# Revit family: HVAC_Fireplaces_Regency-Fireplace_Seattle-Gas-Fireplace_CST50E-3
name_source: partatom
category: Specialty Equipment
units: mm (PartAtom-declared; Revit-internal decimal feet)

## family parameters
Cut with Voids When Loaded = No
Host = Face
Maintain Annotation Orientation = No
OmniClass Number = 23.40.20.34.14
OmniClass Title = Fireplaces
Part Type = Normal
Room Calculation Point = No
Round Connector Dimension = Use Diameter
Shared = No

## types (2) — shared parameters
Apparent Load = 0 VA
Depth = 23 "
Description = The Seattle See-Through 50” model is a stunning addition to our extremely popular City Series Lineup. Enjoy unmatched City Views from two rooms with our first see-through City Series designer gas fireplace. Featuring all the exceptional features of our entire City Series lineup, you can enjoy a frameless view of the fire (now from two sides!), finish direct to the edge of the fireplace with any material and hang TV's or artwork without worry with Regency's patented Cool Wall System.
Duct Connector Description = 5 Inner / 8 Outer
Duct Diameter = 8 "
Exhaust center to stand-off = 12 "
Faceplate Material = Regency Fireplace - Metal - Black
Frequency = 0 Hz
Gas flow = 0.0 L/s
Glass center to standoff = 31 "
Height = 42 "
Housing Material = Regency Fireplace - Metal - Black
Inner Panel Material = Regency Fireplace - Glass - Black Inner Panel
Manufacturer = Regency Fireplace
Nailing strip = 62 "
Number of Poles = 1
Pipe Diameter = 1 "
Power Consumption = 0 W
Power Factor = 1
Product Documentation Link = https://assets.regency-fire.com
Product Page URL = https://www.regency-fire.com
Product data url = https://bimobject.com
URL = https://www.regency-fire.com
Unit base to bottom opening = 10 "
Unit body height = 42 "
Unit body width = 52 "
Unit height = 42 "
Ventilation flow = 0.0 L/s
Version = 1
Viewing opening height = 18 "
Viewing opening width = 49 "
Voltage = 120 V
WIFI Dongle Instal = Yes
Width = 62 "
Width (lip to lip) = 23 "
zero-valued in all types: Default Elevation

## per-type parameters (varying)
| type | CSA P.4.1 | Fuel Type | Gas Connector Description | Gas Flow Minimum Supply Pressure | Manifold Pressure - High | Manifold Pressure - Low | Maximum Input Altitude 0-4500 ft. (0-1372m) | Minimum Input Altitude 0-4500 ft. (0-1372m) | Minimum Supply Pressure | Orifce Size -Altitude 0-4500 ft |
| CST50E-NG | 57.49% | Natural Gas | Natural gas supply | 5" WC/C.E. (0.94kPa) | 3.8” W.C. (0.94 kPa) | 1.1” W.C. (0.27 kPa) | 35,000 Btu/h (10.25 kW) | 19,000Btu/h (5.56 kW) | 5” W.C. (1.25 kPa) | # 36 DMS |
| CST50E-LP | 60.55% | Propane | Propane gas supply | 11" WC/C.E. (0.72 kPa) | 10.5” W.C. (2.62 kPa) | 2.9” W.C. (0.72 kPa) | 33,000 Btu/h (9.66 kW) | 17,000 Btu/h (4.98 kW) | 11” W.C. (2.73 kPa) | # 52 DMS |

note: column(s) folded — value = type name in every type: Model

## geometry (parser evidence)
native form markers: Sweep x2
no freeform markers — native parametric forms only
